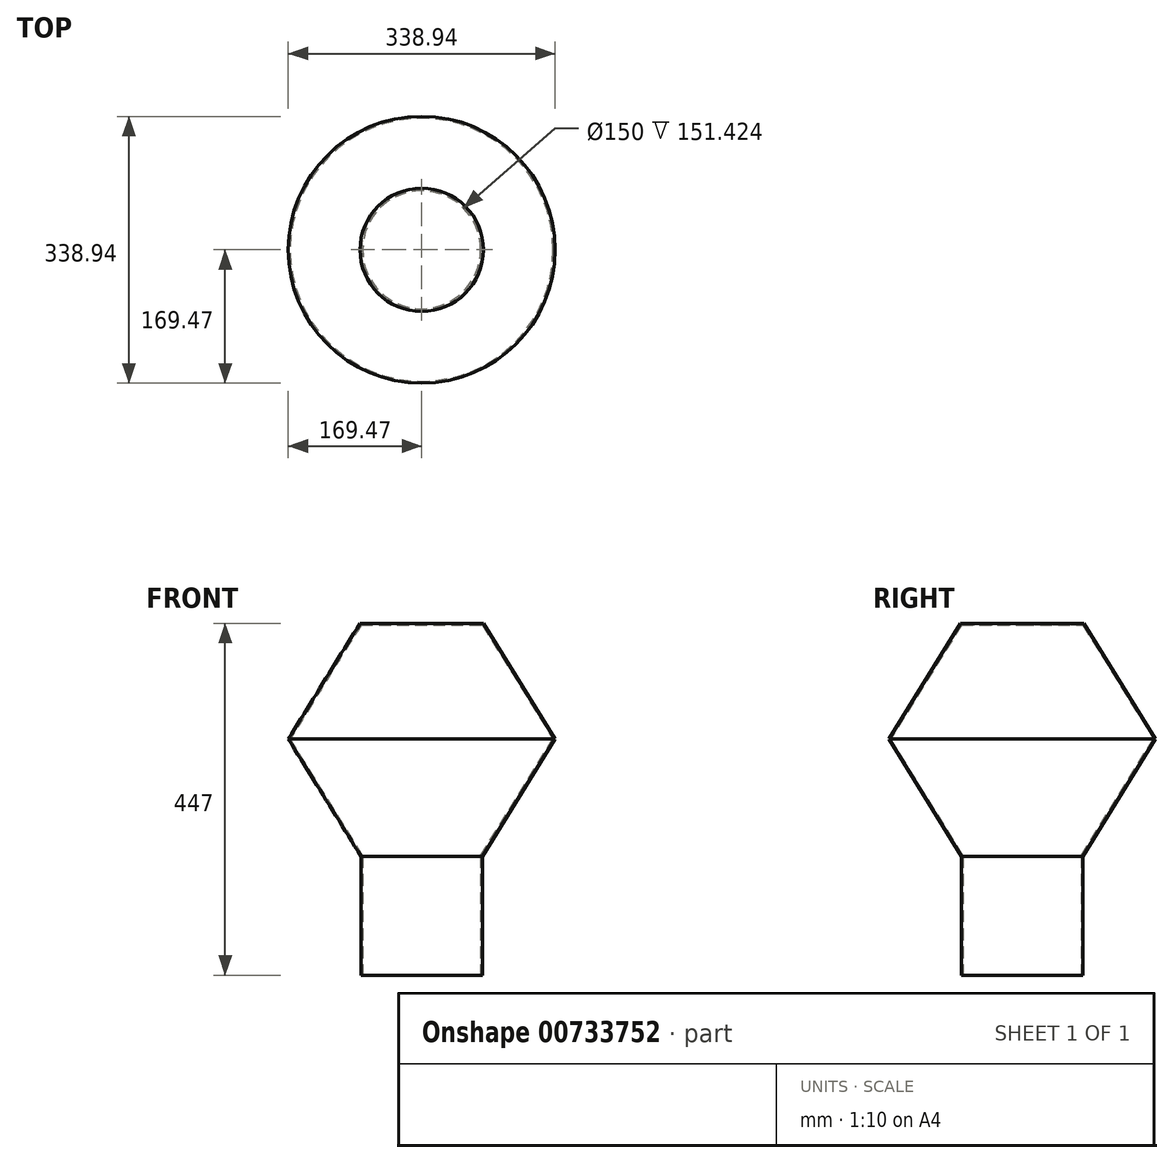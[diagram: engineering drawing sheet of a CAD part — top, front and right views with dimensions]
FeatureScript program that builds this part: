
annotation { "Feature Type Name" : "Feature", "Feature Type Description" : "" }
export const myFeature = defineFeature(function(context is Context, id is Id, definition is map)
    precondition{}
    {
        {
            var Q0;
            Q0=qCreatedBy(makeId("Front.planeOp"),FACE);
            var sketch = newSketch(context, id + "F0", { "sketchPlane" : qUnion([Q0])});
            skLineSegment(sketch, "E0.bottom", {"start": v(0, 0) * mm, "end": v(77, 0) * mm});
            skLineSegment(sketch, "E0.left", {"start": v(0, 0) * mm, "end": v(0, 150) * mm});
            skLineSegment(sketch, "E0.right", {"start": v(77, 0) * mm, "end": v(77, 150.85) * mm});
            skLineSegment(sketch, "E1.left", {"start": v(0, 150) * mm, "end": v(0, 300) * mm});
            skLineSegment(sketch, "E2.top", {"start": v(0, 447) * mm, "end": v(78.33, 447) * mm});
            skLineSegment(sketch, "E2.left", {"start": v(0, 300) * mm, "end": v(0, 447) * mm});
            skLineSegment(sketch, "E3", {"start": v(77, 150.85) * mm, "end": v(169.47, 300) * mm});
            skLineSegment(sketch, "E4", {"start": v(169.47, 300) * mm, "end": v(78.33, 447) * mm});
            skLineSegment(sketch, "E5.0", {"start": v(0, 445) * mm, "end": v(77.22, 445) * mm});
            skLineSegment(sketch, "E5.1", {"start": v(167.12, 300) * mm, "end": v(77.22, 445) * mm});
            skLineSegment(sketch, "E5.2", {"start": v(75, 151.42) * mm, "end": v(167.12, 300) * mm});
            skLineSegment(sketch, "E5.3", {"start": v(75, 0) * mm, "end": v(75, 151.42) * mm});
            skSolve(sketch);
        }
        {
            var Q0;
            {var subQ3=sQuery(id+"F0.wireOp",EDGE,"E0.right");Q0=makeQuery(id+"F0.imprint","IMPRINT",FACE,{"disambiguationData":[TD([[makeQuery(id+"F0.imprint","IMPRINT",EDGE,{"derivedFrom":subQ3}),1.0]])]});}
            var Q1;
            Q1=sQuery(id+"F0.wireOp",EDGE,"E1.left");
            revolve(context, id + "F1", {"surfaceOperationType" : NewSurfaceOperationType.NEW, "entities" : qUnion([Q0]), "axis" : qUnion([Q1]), "revolveType" : RevolveType.FULL});
        }
    });
